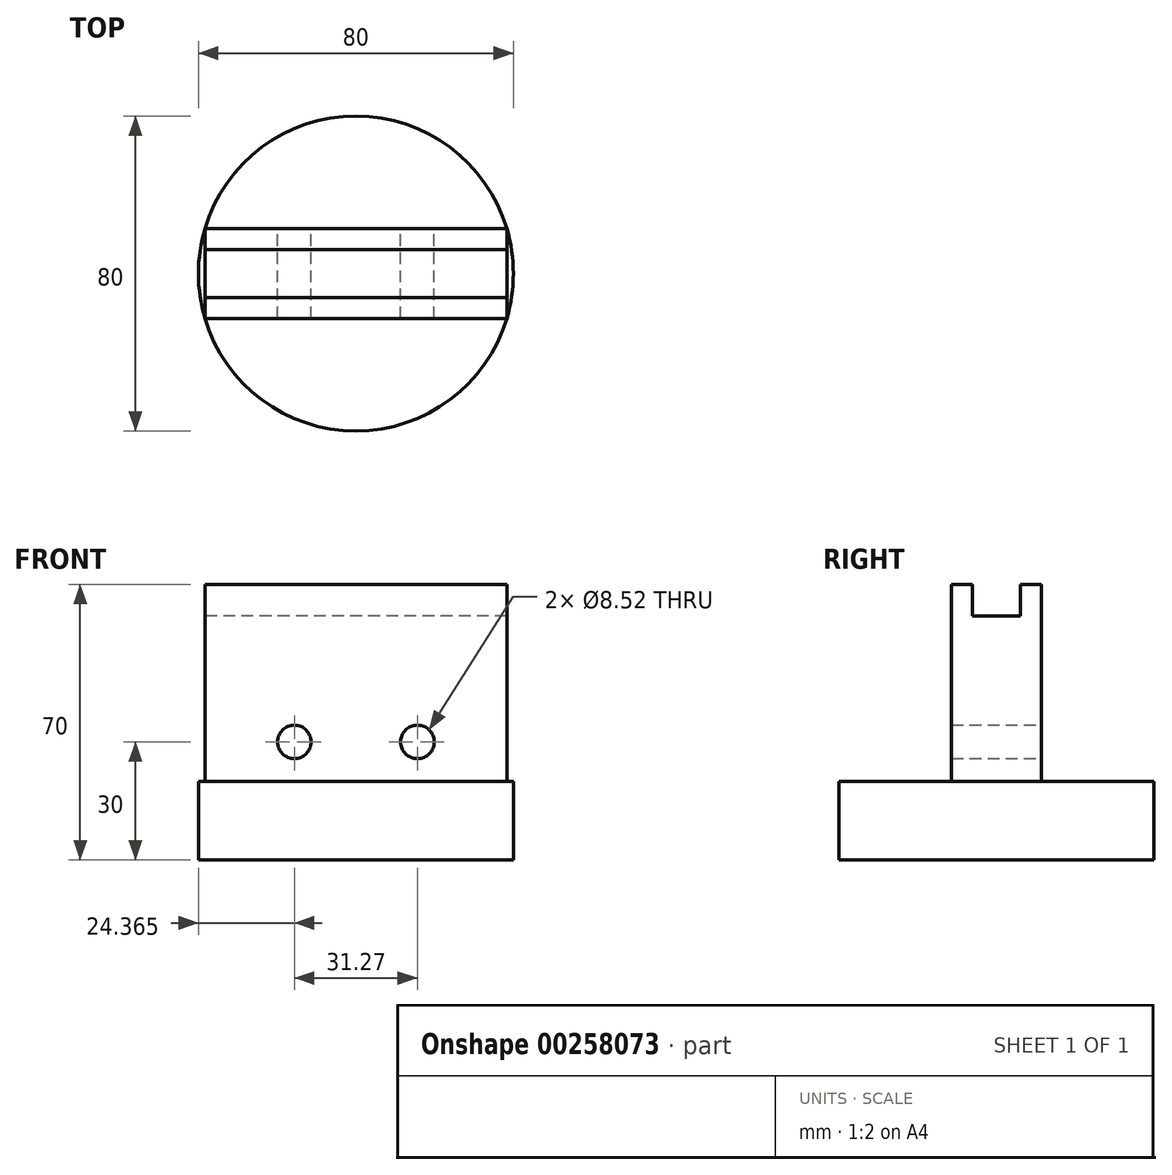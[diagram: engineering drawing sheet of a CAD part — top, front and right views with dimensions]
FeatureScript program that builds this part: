
annotation { "Feature Type Name" : "Feature", "Feature Type Description" : "" }
export const myFeature = defineFeature(function(context is Context, id is Id, definition is map)
    precondition{}
    {
        {
            var Q0;
            Q0=qCreatedBy(makeId("Top.planeOp"),FACE);
            var sketch = newSketch(context, id + "F0", { "sketchPlane" : qUnion([Q0])});
            skCircle(sketch, "E0", {"center": v(0, 0) * mm, "radius": 40 * mm});
            skSolve(sketch);
        }
        {
            var Q0;
            Q0=makeQuery(id+"F0.imprint","IMPRINT",FACE,{"disambiguationData":[TD([[makeQuery(id+"F0.imprint","IMPRINT",EDGE,{"derivedFrom":sQuery(id+"F0.wireOp",EDGE,"E0")}),1.0]])]});
            extrude(context, id + "F1", {"entities" : qUnion([Q0]), "depth" : 20 * mm});
        }
        {
            var Q0;
            Q0=makeQuery(id+"F1.opExtrude","CAP_FACE",FACE,{"disambiguationData":[OSD([sQuery(id+"F0.wireOp",EDGE,"E0")])],"isStart":false});
            var sketch = newSketch(context, id + "F2", { "sketchPlane" : qUnion([Q0])});
            skLineSegment(sketch, "E1.bottom", {"start": v(38.34, -11.4) * mm, "end": v(-38.34, -11.4) * mm});
            skLineSegment(sketch, "E1.top", {"start": v(38.34, 11.4) * mm, "end": v(-38.34, 11.4) * mm});
            skLineSegment(sketch, "E1.left", {"start": v(38.34, -11.4) * mm, "end": v(38.34, 11.4) * mm});
            skLineSegment(sketch, "E1.right", {"start": v(-38.34, -11.4) * mm, "end": v(-38.34, 11.4) * mm});
            skPoint(sketch, "E1.middle", {"position": v(0, 0) * mm});
            skSolve(sketch);
        }
        {
            var Q0;
            Q0=makeQuery(id+"F2.imprint","IMPRINT",FACE,{"disambiguationData":[TD([[makeQuery(id+"F2.imprint","IMPRINT",EDGE,{"derivedFrom":sQuery(id+"F2.wireOp",EDGE,"E1.bottom")}),-1.0]])]});
            extrude(context, id + "F3", {"entities" : qUnion([Q0]), "operationType" : NewBodyOperationType.ADD, "depth" : 50 * mm});
        }
        {
            var Q0;
            Q0=makeQuery(id+"F3.opExtrude","CAP_FACE",FACE,{"disambiguationData":[OSD([sQuery(id+"F2.wireOp",EDGE,"E1.bottom"),sQuery(id+"F2.wireOp",EDGE,"E1.top"),sQuery(id+"F2.wireOp",EDGE,"E1.left"),sQuery(id+"F2.wireOp",EDGE,"E1.right")])],"isStart":false});
            var sketch = newSketch(context, id + "F4", { "sketchPlane" : qUnion([Q0])});
            skLineSegment(sketch, "E2.bottom", {"start": v(38.34, -6.08) * mm, "end": v(-38.34, -6.08) * mm});
            skLineSegment(sketch, "E2.top", {"start": v(38.34, 6.08) * mm, "end": v(-38.34, 6.08) * mm});
            skLineSegment(sketch, "E2.left", {"start": v(38.34, -6.08) * mm, "end": v(38.34, 6.08) * mm});
            skLineSegment(sketch, "E2.right", {"start": v(-38.34, -6.08) * mm, "end": v(-38.34, 6.08) * mm});
            skPoint(sketch, "E2.middle", {"position": v(0, 0) * mm});
            skSolve(sketch);
        }
        {
            var Q0;
            Q0 = qSketchRegion(id + "F4", true);
            extrude(context, id + "F5", {"entities" : qUnion([Q0]), "operationType" : NewBodyOperationType.REMOVE, "oppositeDirection" : true, "depth" : 8 * mm});
        }
        {
            var Q0;
            Q0=makeQuery(id+"F3.opExtrude","SWEPT_FACE",FACE,{"disambiguationData":[OSD([sQuery(id+"F2.wireOp",EDGE,"E1.top")])]});
            var sketch = newSketch(context, id + "F6", { "sketchPlane" : qUnion([Q0])});
            skCircle(sketch, "E3", {"center": v(-15.63, 30) * mm, "radius": 4.26 * mm});
            skCircle(sketch, "E4", {"center": v(15.63, 30) * mm, "radius": 4.26 * mm});
            skSolve(sketch);
        }
        {
            var Q0;
            Q0 = qSketchRegion(id + "F6", true);
            extrude(context, id + "F7", {"entities" : qUnion([Q0]), "operationType" : NewBodyOperationType.REMOVE, "endBound" : BoundingType.THROUGH_ALL, "oppositeDirection" : true, "depth" : 25 * mm});
        }
    });
